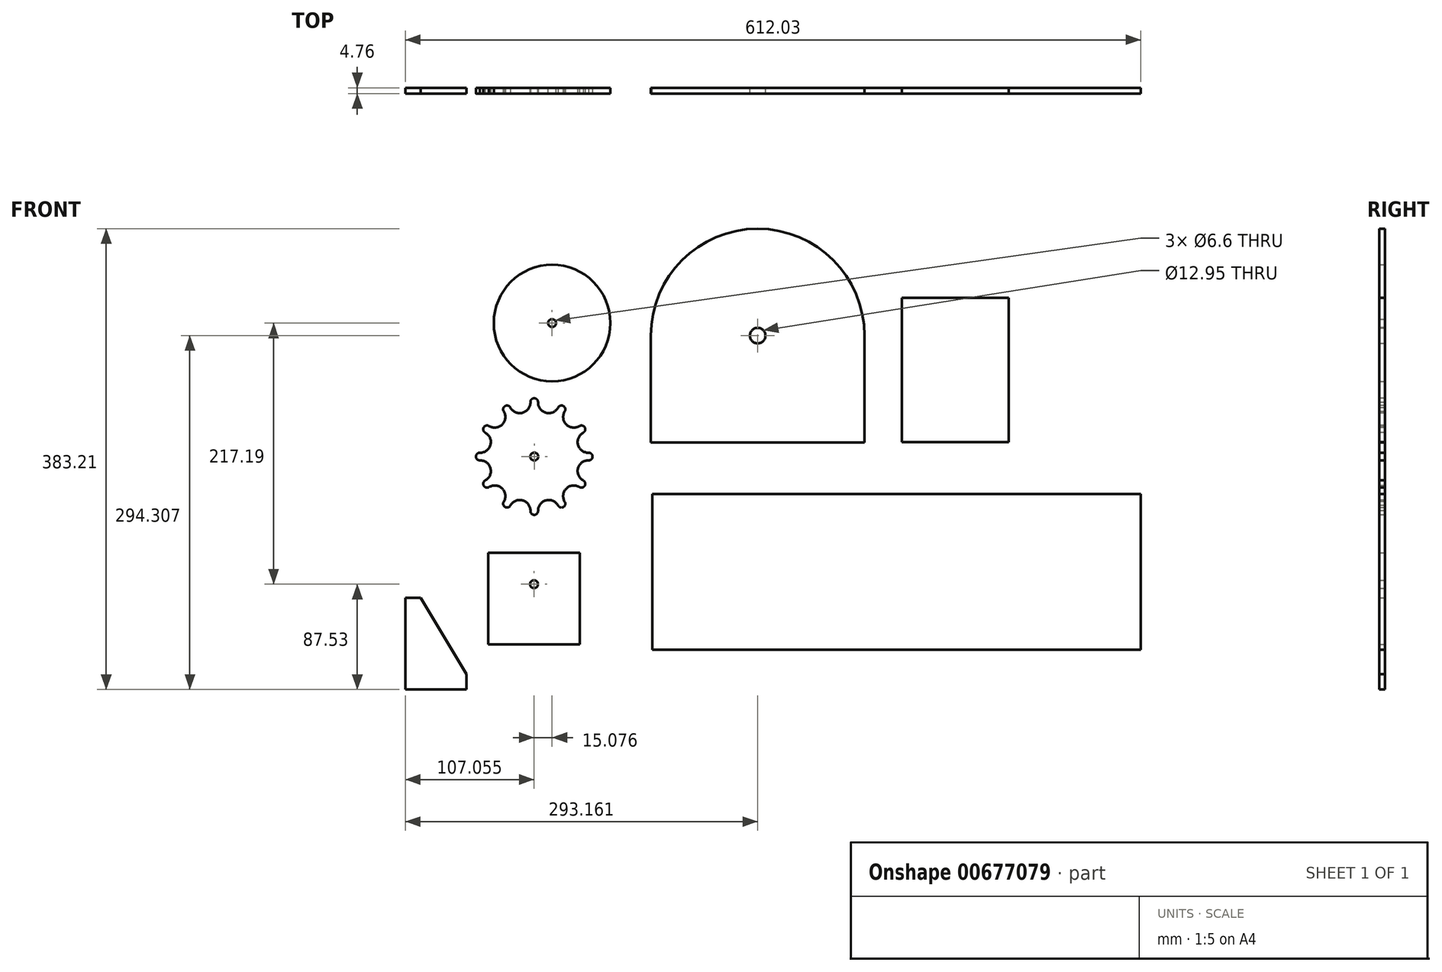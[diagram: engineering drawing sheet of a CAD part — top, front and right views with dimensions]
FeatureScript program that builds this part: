
annotation { "Feature Type Name" : "Feature", "Feature Type Description" : "" }
export const myFeature = defineFeature(function(context is Context, id is Id, definition is map)
    precondition{}
    {
        {
            var Q0;
            Q0=qCreatedBy(makeId("Front.planeOp"),FACE);
            var sketch = newSketch(context, id + "F0", { "sketchPlane" : qUnion([Q0])});
            skCircle(sketch, "E0", {"center": v(-95.15, 44.28) * mm, "radius": 48.51 * mm});
            skCircle(sketch, "E1", {"center": v(-95.15, 44.28) * mm, "radius": 3.3 * mm});
            skCircle(sketch, "E2", {"center": v(-110, -66.75) * mm, "radius": 48.51 * mm});
            skCircle(sketch, "E3", {"center": v(-110, -66.75) * mm, "radius": 3.3 * mm});
            skSolve(sketch);
        }
        {
            var Q0;
            Q0=makeQuery(id+"F0.imprint","IMPRINT",FACE,{"disambiguationData":[TD([[makeQuery(id+"F0.imprint","IMPRINT",EDGE,{"derivedFrom":sQuery(id+"F0.wireOp",EDGE,"E0")}),1.0]])]});
            var Q1;
            Q1=makeQuery(id+"F0.imprint","IMPRINT",FACE,{"disambiguationData":[TD([[makeQuery(id+"F0.imprint","IMPRINT",EDGE,{"derivedFrom":sQuery(id+"F0.wireOp",EDGE,"E2")}),1.0]])]});
            extrude(context, id + "F1", {"entities" : qUnion([Q0, Q1]), "depth" : 4.76 * mm, "offsetDistance" : 25.4 * mm});
        }
        {
            var Q0;
            Q0=makeQuery(id+"F1.opExtrude","CAP_FACE",FACE,{"disambiguationData":[OSD([sQuery(id+"F0.wireOp",EDGE,"E2"),sQuery(id+"F0.wireOp",EDGE,"E3")])],"isStart":false});
            var sketch = newSketch(context, id + "F2", { "sketchPlane" : qUnion([Q0])});
            skCircle(sketch, "E4", {"center": v(-110, -66.75) * mm, "radius": 48.51 * mm});
            skLineSegment(sketch, "E5", {"start": v(-110, -66.75) * mm, "end": v(-110, -18.24) * mm});
            skLineSegment(sketch, "E6", {"start": v(-110, -66.75) * mm, "end": v(-110, -115.26) * mm});
            skLineSegment(sketch, "E7", {"start": v(-110, -66.75) * mm, "end": v(-152.02, -42.5) * mm});
            skLineSegment(sketch, "E8", {"start": v(-110, -66.75) * mm, "end": v(-152.02, -91) * mm});
            skLineSegment(sketch, "E9", {"start": v(-110, -66.75) * mm, "end": v(-158.52, -66.75) * mm});
            skLineSegment(sketch, "E10", {"start": v(-110, -66.75) * mm, "end": v(-134.26, -24.74) * mm});
            skLineSegment(sketch, "E11", {"start": v(-110, -66.75) * mm, "end": v(-134.26, -108.76) * mm});
            skCircle(sketch, "E12", {"center": v(-149.27, -44.08) * mm, "radius": 3.18 * mm});
            skCircle(sketch, "E13", {"center": v(-132.68, -27.49) * mm, "radius": 3.18 * mm});
            skLineSegment(sketch, "E14", {"start": v(-132.68, -27.49) * mm, "end": v(-135.43, -29.08) * mm});
            skLineSegment(sketch, "E15", {"start": v(-149.27, -44.08) * mm, "end": v(-147.68, -41.33) * mm});
            skArc(sketch, "E16", {"start": v(-147.68, -41.33) * mm, "mid": v(-136.67, -40.1) * mm, "end": v(-135.43, -29.08) * mm});
            skCircle(sketch, "E17", {"center": v(-110, -21.41) * mm, "radius": 3.18 * mm});
            skCircle(sketch, "E18", {"center": v(-155.34, -66.75) * mm, "radius": 3.18 * mm});
            skCircle(sketch, "E19", {"center": v(-149.27, -89.42) * mm, "radius": 3.18 * mm});
            skCircle(sketch, "E20", {"center": v(-132.68, -106.01) * mm, "radius": 3.18 * mm});
            skLineSegment(sketch, "E21", {"start": v(-149.27, -44.08) * mm, "end": v(-150.86, -46.83) * mm});
            skLineSegment(sketch, "E22", {"start": v(-155.34, -66.75) * mm, "end": v(-155.34, -63.57) * mm});
            skLineSegment(sketch, "E23", {"start": v(-155.34, -66.75) * mm, "end": v(-155.34, -69.92) * mm});
            skLineSegment(sketch, "E24", {"start": v(-149.27, -89.42) * mm, "end": v(-150.86, -86.67) * mm});
            skLineSegment(sketch, "E25", {"start": v(-149.27, -89.42) * mm, "end": v(-147.68, -92.17) * mm});
            skLineSegment(sketch, "E26", {"start": v(-132.68, -106.01) * mm, "end": v(-135.43, -104.42) * mm});
            skLineSegment(sketch, "E27", {"start": v(-132.68, -106.01) * mm, "end": v(-129.93, -107.6) * mm});
            skArc(sketch, "E28", {"start": v(-155.34, -63.57) * mm, "mid": v(-146.43, -57) * mm, "end": v(-150.86, -46.83) * mm});
            skArc(sketch, "E29", {"start": v(-150.86, -86.67) * mm, "mid": v(-146.43, -76.5) * mm, "end": v(-155.34, -69.92) * mm});
            skArc(sketch, "E30", {"start": v(-135.43, -104.42) * mm, "mid": v(-136.67, -93.4) * mm, "end": v(-147.68, -92.17) * mm});
            skLineSegment(sketch, "E31", {"start": v(-110, -21.41) * mm, "end": v(-113.18, -21.41) * mm});
            skCircle(sketch, "E32", {"center": v(-110, -112.08) * mm, "radius": 3.18 * mm});
            skLineSegment(sketch, "E33", {"start": v(-110, -112.08) * mm, "end": v(-113.18, -112.08) * mm});
            skArc(sketch, "E34", {"start": v(-113.18, -112.08) * mm, "mid": v(-119.77, -103.17) * mm, "end": v(-129.93, -107.6) * mm});
            skLineSegment(sketch, "E35", {"start": v(-132.68, -27.49) * mm, "end": v(-129.93, -25.9) * mm});
            skArc(sketch, "E36", {"start": v(-129.93, -25.9) * mm, "mid": v(-119.77, -30.33) * mm, "end": v(-113.18, -21.41) * mm});
            skArc(sketch, "E37.MirrorCS", {"start": v(-90.1, -25.9) * mm, "mid": v(-100.25, -30.33) * mm, "end": v(-106.83, -21.41) * mm});
            skCircle(sketch, "E38.MirrorC", {"center": v(-87.34, -27.49) * mm, "radius": 3.18 * mm});
            skArc(sketch, "E39.MirrorCS", {"start": v(-72.34, -41.33) * mm, "mid": v(-83.35, -40.1) * mm, "end": v(-84.6, -29.08) * mm});
            skCircle(sketch, "E40.MirrorC", {"center": v(-70.75, -44.08) * mm, "radius": 3.18 * mm});
            skArc(sketch, "E41.MirrorCS", {"start": v(-64.67, -63.57) * mm, "mid": v(-73.6, -57) * mm, "end": v(-69.16, -46.83) * mm});
            skCircle(sketch, "E42.MirrorC", {"center": v(-64.67, -66.75) * mm, "radius": 3.18 * mm});
            skArc(sketch, "E43.MirrorCS", {"start": v(-69.16, -86.67) * mm, "mid": v(-73.6, -76.5) * mm, "end": v(-64.67, -69.92) * mm});
            skCircle(sketch, "E44.MirrorC", {"center": v(-70.75, -89.42) * mm, "radius": 3.18 * mm});
            skArc(sketch, "E45.MirrorCS", {"start": v(-84.6, -104.42) * mm, "mid": v(-83.35, -93.4) * mm, "end": v(-72.34, -92.17) * mm});
            skCircle(sketch, "E46.MirrorC", {"center": v(-87.34, -106.01) * mm, "radius": 3.18 * mm});
            skArc(sketch, "E47.MirrorCS", {"start": v(-106.83, -112.08) * mm, "mid": v(-100.25, -103.17) * mm, "end": v(-90.1, -107.6) * mm});
            skSolve(sketch);
        }
        {
            var Q0;
            {var subQ3=sQuery(id+"F2.wireOp",EDGE,"E16");var subQ5=sQuery(id+"F2.wireOp",EDGE,"E12");var subQ8=makeQuery(id+"F2.imprint","INTERSECT",VERTEX,{"derivedFrom":[subQ5,subQ3]});Q0=makeQuery(id+"F2.imprint","IMPRINT",FACE,{"disambiguationData":[TD([[makeQuery(id+"F2.imprint","IMPRINT",EDGE,{"disambiguationData":[TD([[subQ8,-1.0]])],"derivedFrom":subQ3}),1.0]])]});}
            var Q1;
            {var subQ0=sQuery(id+"F2.wireOp",EDGE,"E13");var subQ3=sQuery(id+"F2.wireOp",EDGE,"E36");var subQ8=makeQuery(id+"F2.imprint","INTERSECT",VERTEX,{"derivedFrom":[subQ0,subQ3]});Q1=makeQuery(id+"F2.imprint","IMPRINT",FACE,{"disambiguationData":[TD([[makeQuery(id+"F2.imprint","IMPRINT",EDGE,{"disambiguationData":[TD([[subQ8,-1.0]])],"derivedFrom":subQ3}),1.0]])]});}
            var Q2;
            {var subQ0=sQuery(id+"F2.wireOp",EDGE,"E37.MirrorCS");var subQ1=sQuery(id+"F2.wireOp",EDGE,"E17");var subQ5=makeQuery(id+"F2.imprint","INTERSECT",VERTEX,{"disambiguationData":[OD(0.0)],"derivedFrom":[subQ1,subQ0]});Q2=makeQuery(id+"F2.imprint","IMPRINT",FACE,{"disambiguationData":[TD([[makeQuery(id+"F2.imprint","IMPRINT",EDGE,{"disambiguationData":[TD([[subQ5,1.0]])],"derivedFrom":subQ1}),-1.0]])]});}
            var Q3;
            {var subQ4=sQuery(id+"F2.wireOp",EDGE,"E4");var subQ6=sQuery(id+"F2.wireOp",EDGE,"E40.MirrorC");var subQ8=makeQuery(id+"F2.imprint","INTERSECT",VERTEX,{"derivedFrom":[subQ4,subQ6]});Q3=makeQuery(id+"F2.imprint","IMPRINT",FACE,{"disambiguationData":[TD([[makeQuery(id+"F2.imprint","IMPRINT",EDGE,{"disambiguationData":[TD([[subQ8,-1.0]])],"derivedFrom":subQ4}),1.0]])]});}
            var Q4;
            {var subQ1=sQuery(id+"F2.wireOp",EDGE,"E40.MirrorC");var subQ6=sQuery(id+"F2.wireOp",EDGE,"E4");var subQ7=makeQuery(id+"F2.imprint","INTERSECT",VERTEX,{"derivedFrom":[subQ6,subQ1]});Q4=makeQuery(id+"F2.imprint","IMPRINT",FACE,{"disambiguationData":[TD([[makeQuery(id+"F2.imprint","IMPRINT",EDGE,{"disambiguationData":[TD([[subQ7,1.0]])],"derivedFrom":subQ6}),1.0]])]});}
            var Q5;
            {var subQ1=sQuery(id+"F2.wireOp",EDGE,"E42.MirrorC");var subQ6=sQuery(id+"F2.wireOp",EDGE,"E4");var subQ7=makeQuery(id+"F2.imprint","INTERSECT",VERTEX,{"derivedFrom":[subQ6,subQ1]});Q5=makeQuery(id+"F2.imprint","IMPRINT",FACE,{"disambiguationData":[TD([[makeQuery(id+"F2.imprint","IMPRINT",EDGE,{"disambiguationData":[TD([[subQ7,1.0]])],"derivedFrom":subQ6}),1.0]])]});}
            var Q6;
            {var subQ4=sQuery(id+"F2.wireOp",EDGE,"E46.MirrorC");var subQ5=sQuery(id+"F2.wireOp",EDGE,"E4");var subQ6=makeQuery(id+"F2.imprint","INTERSECT",VERTEX,{"derivedFrom":[subQ5,subQ4]});Q6=makeQuery(id+"F2.imprint","IMPRINT",FACE,{"disambiguationData":[TD([[makeQuery(id+"F2.imprint","IMPRINT",EDGE,{"disambiguationData":[TD([[subQ6,-1.0]])],"derivedFrom":subQ5}),1.0]])]});}
            var Q7;
            {var subQ0=sQuery(id+"F2.wireOp",EDGE,"E32");var subQ3=sQuery(id+"F2.wireOp",EDGE,"E47.MirrorCS");var subQ4=makeQuery(id+"F2.imprint","INTERSECT",VERTEX,{"disambiguationData":[OD(0.0)],"derivedFrom":[subQ0,subQ3]});Q7=makeQuery(id+"F2.imprint","IMPRINT",FACE,{"disambiguationData":[TD([[makeQuery(id+"F2.imprint","IMPRINT",EDGE,{"disambiguationData":[TD([[subQ4,-1.0]])],"derivedFrom":subQ0}),-1.0]])]});}
            var Q8;
            {var subQ0=sQuery(id+"F2.wireOp",EDGE,"E34");var subQ4=sQuery(id+"F2.wireOp",EDGE,"E20");var subQ6=makeQuery(id+"F2.imprint","INTERSECT",VERTEX,{"derivedFrom":[subQ4,subQ0]});Q8=makeQuery(id+"F2.imprint","IMPRINT",FACE,{"disambiguationData":[TD([[makeQuery(id+"F2.imprint","IMPRINT",EDGE,{"disambiguationData":[TD([[subQ6,1.0]])],"derivedFrom":subQ0}),1.0]])]});}
            var Q9;
            {var subQ0=sQuery(id+"F2.wireOp",EDGE,"E30");var subQ4=sQuery(id+"F2.wireOp",EDGE,"E19");var subQ6=makeQuery(id+"F2.imprint","INTERSECT",VERTEX,{"derivedFrom":[subQ4,subQ0]});Q9=makeQuery(id+"F2.imprint","IMPRINT",FACE,{"disambiguationData":[TD([[makeQuery(id+"F2.imprint","IMPRINT",EDGE,{"disambiguationData":[TD([[subQ6,1.0]])],"derivedFrom":subQ0}),1.0]])]});}
            var Q10;
            {var subQ0=sQuery(id+"F2.wireOp",EDGE,"E29");var subQ4=sQuery(id+"F2.wireOp",EDGE,"E18");var subQ5=makeQuery(id+"F2.imprint","INTERSECT",VERTEX,{"derivedFrom":[subQ4,subQ0]});Q10=makeQuery(id+"F2.imprint","IMPRINT",FACE,{"disambiguationData":[TD([[makeQuery(id+"F2.imprint","IMPRINT",EDGE,{"disambiguationData":[TD([[subQ5,1.0]])],"derivedFrom":subQ0}),1.0]])]});}
            var Q11;
            {var subQ0=sQuery(id+"F2.wireOp",EDGE,"E28");var subQ4=sQuery(id+"F2.wireOp",EDGE,"E12");var subQ8=makeQuery(id+"F2.imprint","INTERSECT",VERTEX,{"derivedFrom":[subQ4,subQ0]});Q11=makeQuery(id+"F2.imprint","IMPRINT",FACE,{"disambiguationData":[TD([[makeQuery(id+"F2.imprint","IMPRINT",EDGE,{"disambiguationData":[TD([[subQ8,1.0]])],"derivedFrom":subQ0}),1.0]])]});}
            extrude(context, id + "F3", {"entities" : qUnion([Q0, Q1, Q2, Q3, Q4, Q5, Q6, Q7, Q8, Q9, Q10, Q11]), "operationType" : NewBodyOperationType.REMOVE, "endBound" : BoundingType.THROUGH_ALL, "oppositeDirection" : true, "depth" : 25.4 * mm, "offsetDistance" : 25.4 * mm});
        }
        {
            var Q0;
            Q0=qCreatedBy(makeId("Front.planeOp"),FACE);
            var sketch = newSketch(context, id + "F4", { "sketchPlane" : qUnion([Q0])});
            skCircle(sketch, "E48", {"center": v(75.88, 33.87) * mm, "radius": 88.9 * mm});
            skLineSegment(sketch, "E49.bottom", {"start": v(-13.02, 33.87) * mm, "end": v(164.78, 33.87) * mm});
            skLineSegment(sketch, "E49.top", {"start": v(-13.02, -55.03) * mm, "end": v(164.78, -55.03) * mm});
            skLineSegment(sketch, "E49.left", {"start": v(-13.02, 33.87) * mm, "end": v(-13.02, -55.03) * mm});
            skLineSegment(sketch, "E49.right", {"start": v(164.78, 33.87) * mm, "end": v(164.78, -55.03) * mm});
            skCircle(sketch, "E50", {"center": v(75.88, 33.87) * mm, "radius": 6.48 * mm});
            skSolve(sketch);
        }
        {
            var Q0;
            {var subQ0=sQuery(id+"F4.wireOp",EDGE,"E49.bottom");var subQ3=sQuery(id+"F4.wireOp",EDGE,"E50");var subQ6=makeQuery(id+"F4.imprint","INTERSECT",VERTEX,{"disambiguationData":[OD(0.0)],"derivedFrom":[subQ0,subQ3]});Q0=makeQuery(id+"F4.imprint","IMPRINT",FACE,{"disambiguationData":[TD([[makeQuery(id+"F4.imprint","IMPRINT",EDGE,{"disambiguationData":[TD([[subQ6,-1.0]])],"derivedFrom":subQ3}),-1.0]])]});}
            var Q1;
            {var subQ0=sQuery(id+"F4.wireOp",EDGE,"E49.bottom");var subQ4=sQuery(id+"F4.wireOp",EDGE,"E50");var subQ6=makeQuery(id+"F4.imprint","INTERSECT",VERTEX,{"disambiguationData":[OD(0.0)],"derivedFrom":[subQ0,subQ4]});Q1=makeQuery(id+"F4.imprint","IMPRINT",FACE,{"disambiguationData":[TD([[makeQuery(id+"F4.imprint","IMPRINT",EDGE,{"disambiguationData":[TD([[subQ6,1.0]])],"derivedFrom":subQ4}),-1.0]])]});}
            var Q2;
            {var subQ0=sQuery(id+"F4.wireOp",EDGE,"E49.left");Q2=makeQuery(id+"F4.imprint","IMPRINT",FACE,{"disambiguationData":[TD([[makeQuery(id+"F4.imprint","IMPRINT",EDGE,{"derivedFrom":subQ0}),1.0]])]});}
            var Q3;
            {var subQ0=sQuery(id+"F4.wireOp",EDGE,"E49.right");Q3=makeQuery(id+"F4.imprint","IMPRINT",FACE,{"disambiguationData":[TD([[makeQuery(id+"F4.imprint","IMPRINT",EDGE,{"derivedFrom":subQ0}),-1.0]])]});}
            extrude(context, id + "F5", {"entities" : qUnion([Q0, Q1, Q2, Q3]), "depth" : 4.76 * mm, "offsetDistance" : 25.4 * mm});
        }
        {
            var Q0;
            Q0=qCreatedBy(makeId("Front.planeOp"),FACE);
            var sketch = newSketch(context, id + "F6", { "sketchPlane" : qUnion([Q0])});
            skLineSegment(sketch, "E51.bottom", {"start": v(-11.65, -98.04) * mm, "end": v(394.75, -98.04) * mm});
            skLineSegment(sketch, "E51.top", {"start": v(-11.65, -227.58) * mm, "end": v(394.75, -227.58) * mm});
            skLineSegment(sketch, "E51.left", {"start": v(-11.65, -98.04) * mm, "end": v(-11.65, -227.58) * mm});
            skLineSegment(sketch, "E51.right", {"start": v(394.75, -98.04) * mm, "end": v(394.75, -227.58) * mm});
            skSolve(sketch);
        }
        {
            var Q0;
            Q0=makeQuery(id+"F6.imprint","IMPRINT",FACE,{"disambiguationData":[TD([[makeQuery(id+"F6.imprint","IMPRINT",EDGE,{"derivedFrom":sQuery(id+"F6.wireOp",EDGE,"E51.bottom")}),-1.0]])]});
            extrude(context, id + "F7", {"entities" : qUnion([Q0]), "depth" : 4.76 * mm, "offsetDistance" : 25.4 * mm});
        }
        {
            var Q0;
            Q0=qCreatedBy(makeId("Front.planeOp"),FACE);
            var sketch = newSketch(context, id + "F8", { "sketchPlane" : qUnion([Q0])});
            skLineSegment(sketch, "E52.bottom", {"start": v(195.88, 65.4) * mm, "end": v(284.78, 65.4) * mm});
            skLineSegment(sketch, "E52.top", {"start": v(195.88, -54.62) * mm, "end": v(284.78, -54.62) * mm});
            skLineSegment(sketch, "E52.left", {"start": v(195.88, 65.4) * mm, "end": v(195.88, -54.62) * mm});
            skLineSegment(sketch, "E52.right", {"start": v(284.78, 65.4) * mm, "end": v(284.78, -54.62) * mm});
            skSolve(sketch);
        }
        {
            var Q0;
            Q0=makeQuery(id+"F8.imprint","IMPRINT",FACE,{"disambiguationData":[TD([[makeQuery(id+"F8.imprint","IMPRINT",EDGE,{"derivedFrom":sQuery(id+"F8.wireOp",EDGE,"E52.bottom")}),-1.0]])]});
            extrude(context, id + "F9", {"entities" : qUnion([Q0]), "depth" : 4.76 * mm, "offsetDistance" : 25.4 * mm});
        }
        {
            var Q0;
            Q0=qCreatedBy(makeId("Front.planeOp"),FACE);
            var sketch = newSketch(context, id + "F10", { "sketchPlane" : qUnion([Q0])});
            skLineSegment(sketch, "E53.bottom", {"start": v(-110.22, -146.65) * mm, "end": v(-110.22, -146.65) * mm});
            skLineSegment(sketch, "E53.top", {"start": v(-148.32, -222.85) * mm, "end": v(-72.12, -222.85) * mm});
            skLineSegment(sketch, "E53.left", {"start": v(-148.32, -184.75) * mm, "end": v(-148.32, -222.85) * mm});
            skLineSegment(sketch, "E53.right", {"start": v(-72.12, -184.75) * mm, "end": v(-72.12, -222.85) * mm});
            skArc(sketch, "E54.filletArc", {"start": v(-110.22, -146.65) * mm, "mid": v(-137.17, -157.8) * mm, "end": v(-148.32, -184.75) * mm});
            skArc(sketch, "E55.filletArc", {"start": v(-72.12, -184.75) * mm, "mid": v(-83.28, -157.8) * mm, "end": v(-110.22, -146.65) * mm});
            skCircle(sketch, "E56", {"center": v(-110.22, -172.9) * mm, "radius": 3.3 * mm});
            skLineSegment(sketch, "E57.bottom", {"start": v(-148.32, -184.75) * mm, "end": v(-72.12, -184.75) * mm});
            skLineSegment(sketch, "E57.top", {"start": v(-148.32, -146.65) * mm, "end": v(-72.12, -146.65) * mm});
            skLineSegment(sketch, "E57.left", {"start": v(-148.32, -184.75) * mm, "end": v(-148.32, -146.65) * mm});
            skLineSegment(sketch, "E57.right", {"start": v(-72.12, -184.75) * mm, "end": v(-72.12, -146.65) * mm});
            skSolve(sketch);
        }
        {
            var Q0;
            Q0=makeQuery(id+"F10.imprint","IMPRINT",FACE,{"disambiguationData":[TD([[makeQuery(id+"F10.imprint","IMPRINT",EDGE,{"derivedFrom":sQuery(id+"F10.wireOp",EDGE,"E53.top")}),1.0]])]});
            var Q1;
            {var subQ0=sQuery(id+"F10.wireOp",EDGE,"E54.filletArc");Q1=makeQuery(id+"F10.imprint","IMPRINT",FACE,{"disambiguationData":[TD([[makeQuery(id+"F10.imprint","IMPRINT",EDGE,{"derivedFrom":subQ0}),-1.0]])]});}
            var Q2;
            Q2=makeQuery(id+"F10.imprint","IMPRINT",FACE,{"disambiguationData":[TD([[makeQuery(id+"F10.imprint","IMPRINT",EDGE,{"derivedFrom":sQuery(id+"F10.wireOp",EDGE,"E54.filletArc")}),1.0]])]});
            var Q3;
            {var subQ0=sQuery(id+"F10.wireOp",EDGE,"E55.filletArc");Q3=makeQuery(id+"F10.imprint","IMPRINT",FACE,{"disambiguationData":[TD([[makeQuery(id+"F10.imprint","IMPRINT",EDGE,{"derivedFrom":subQ0}),-1.0]])]});}
            extrude(context, id + "F11", {"entities" : qUnion([Q0, Q1, Q2, Q3]), "depth" : 4.76 * mm, "offsetDistance" : 25.4 * mm});
        }
        {
            var Q0;
            Q0=qCreatedBy(makeId("Front.planeOp"),FACE);
            var sketch = newSketch(context, id + "F12", { "sketchPlane" : qUnion([Q0])});
            skLineSegment(sketch, "E58", {"start": v(-217.28, -260.44) * mm, "end": v(-166.48, -260.44) * mm});
            skLineSegment(sketch, "E59", {"start": v(-166.48, -260.44) * mm, "end": v(-166.48, -247.74) * mm});
            skLineSegment(sketch, "E60", {"start": v(-166.48, -247.74) * mm, "end": v(-204.58, -184.24) * mm});
            skLineSegment(sketch, "E61", {"start": v(-204.58, -184.24) * mm, "end": v(-217.28, -184.24) * mm});
            skLineSegment(sketch, "E62", {"start": v(-217.28, -184.24) * mm, "end": v(-217.28, -260.44) * mm});
            skSolve(sketch);
        }
        {
            var Q0;
            Q0=makeQuery(id+"F12.imprint","IMPRINT",FACE,{"disambiguationData":[TD([[makeQuery(id+"F12.imprint","IMPRINT",EDGE,{"derivedFrom":sQuery(id+"F12.wireOp",EDGE,"E58")}),1.0]])]});
            extrude(context, id + "F13", {"entities" : qUnion([Q0]), "depth" : 4.76 * mm, "offsetDistance" : 25.4 * mm});
        }
    });
